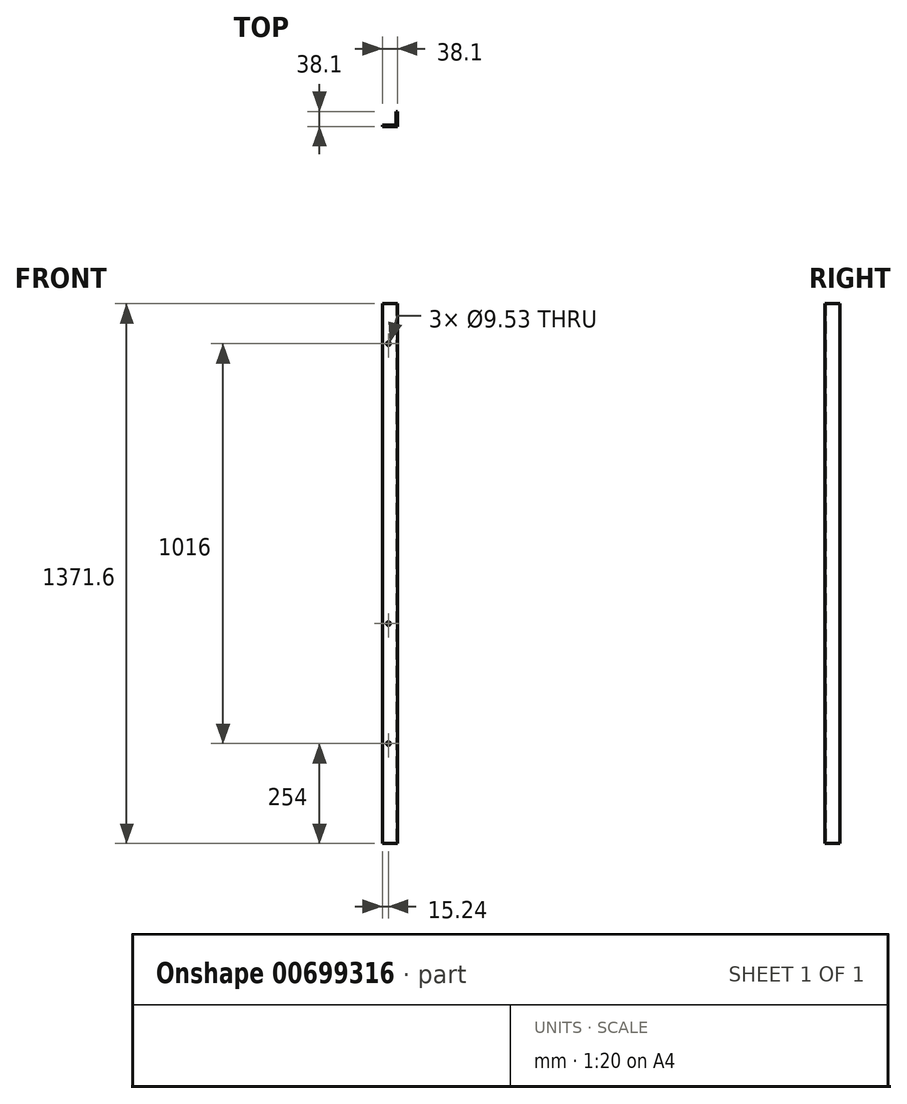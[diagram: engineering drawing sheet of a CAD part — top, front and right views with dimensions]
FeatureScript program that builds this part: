
annotation { "Feature Type Name" : "Feature", "Feature Type Description" : "" }
export const myFeature = defineFeature(function(context is Context, id is Id, definition is map)
    precondition{}
    {
        {
            var Q0;
            Q0=qCreatedBy(makeId("Top.planeOp"),FACE);
            var sketch = newSketch(context, id + "F0", { "sketchPlane" : qUnion([Q0])});
            skLineSegment(sketch, "E0", {"start": v(0, 0) * mm, "end": v(38.1, 0) * mm});
            skLineSegment(sketch, "E1", {"start": v(38.1, 0) * mm, "end": v(38.1, 38.1) * mm});
            skLineSegment(sketch, "E2", {"start": v(38.1, 38.1) * mm, "end": v(34.92, 38.1) * mm});
            skLineSegment(sketch, "E3", {"start": v(34.92, 38.1) * mm, "end": v(34.93, 3.18) * mm});
            skLineSegment(sketch, "E4", {"start": v(34.93, 3.18) * mm, "end": v(0, 3.18) * mm});
            skLineSegment(sketch, "E5", {"start": v(0, 3.18) * mm, "end": v(0, 0) * mm});
            skSolve(sketch);
        }
        {
            var Q0;
            Q0=makeQuery(id+"F0.imprint","IMPRINT",FACE,{"disambiguationData":[TD([[makeQuery(id+"F0.imprint","IMPRINT",EDGE,{"derivedFrom":sQuery(id+"F0.wireOp",EDGE,"E0")}),1.0]])]});
            extrude(context, id + "F1", {"entities" : qUnion([Q0]), "depth" : 1371.6 * mm, "offsetDistance" : 25.4 * mm});
        }
        {
            var Q0;
            Q0=makeQuery(id+"F1.opExtrude","SWEPT_FACE",FACE,{"disambiguationData":[OSD([sQuery(id+"F0.wireOp",EDGE,"E0")])]});
            var sketch = newSketch(context, id + "F2", { "sketchPlane" : qUnion([Q0])});
            skCircle(sketch, "E6", {"center": v(15.24, 1270) * mm, "radius": 4.76 * mm});
            skCircle(sketch, "E7", {"center": v(15.24, 558.8) * mm, "radius": 4.76 * mm});
            skCircle(sketch, "E8", {"center": v(15.24, 254) * mm, "radius": 4.76 * mm});
            skSolve(sketch);
        }
        {
            var Q0;
            Q0=makeQuery(id+"F2.imprint","IMPRINT",FACE,{"disambiguationData":[TD([[makeQuery(id+"F2.imprint","IMPRINT",EDGE,{"derivedFrom":sQuery(id+"F2.wireOp",EDGE,"E8")}),1.0]])]});
            var Q1;
            Q1=makeQuery(id+"F2.imprint","IMPRINT",FACE,{"disambiguationData":[TD([[makeQuery(id+"F2.imprint","IMPRINT",EDGE,{"derivedFrom":sQuery(id+"F2.wireOp",EDGE,"E7")}),1.0]])]});
            var Q2;
            Q2=makeQuery(id+"F2.imprint","IMPRINT",FACE,{"disambiguationData":[TD([[makeQuery(id+"F2.imprint","IMPRINT",EDGE,{"derivedFrom":sQuery(id+"F2.wireOp",EDGE,"E6")}),1.0]])]});
            extrude(context, id + "F3", {"entities" : qUnion([Q0, Q1, Q2]), "operationType" : NewBodyOperationType.REMOVE, "endBound" : BoundingType.THROUGH_ALL, "oppositeDirection" : true, "depth" : 25.4 * mm, "offsetDistance" : 25.4 * mm});
        }
    });
